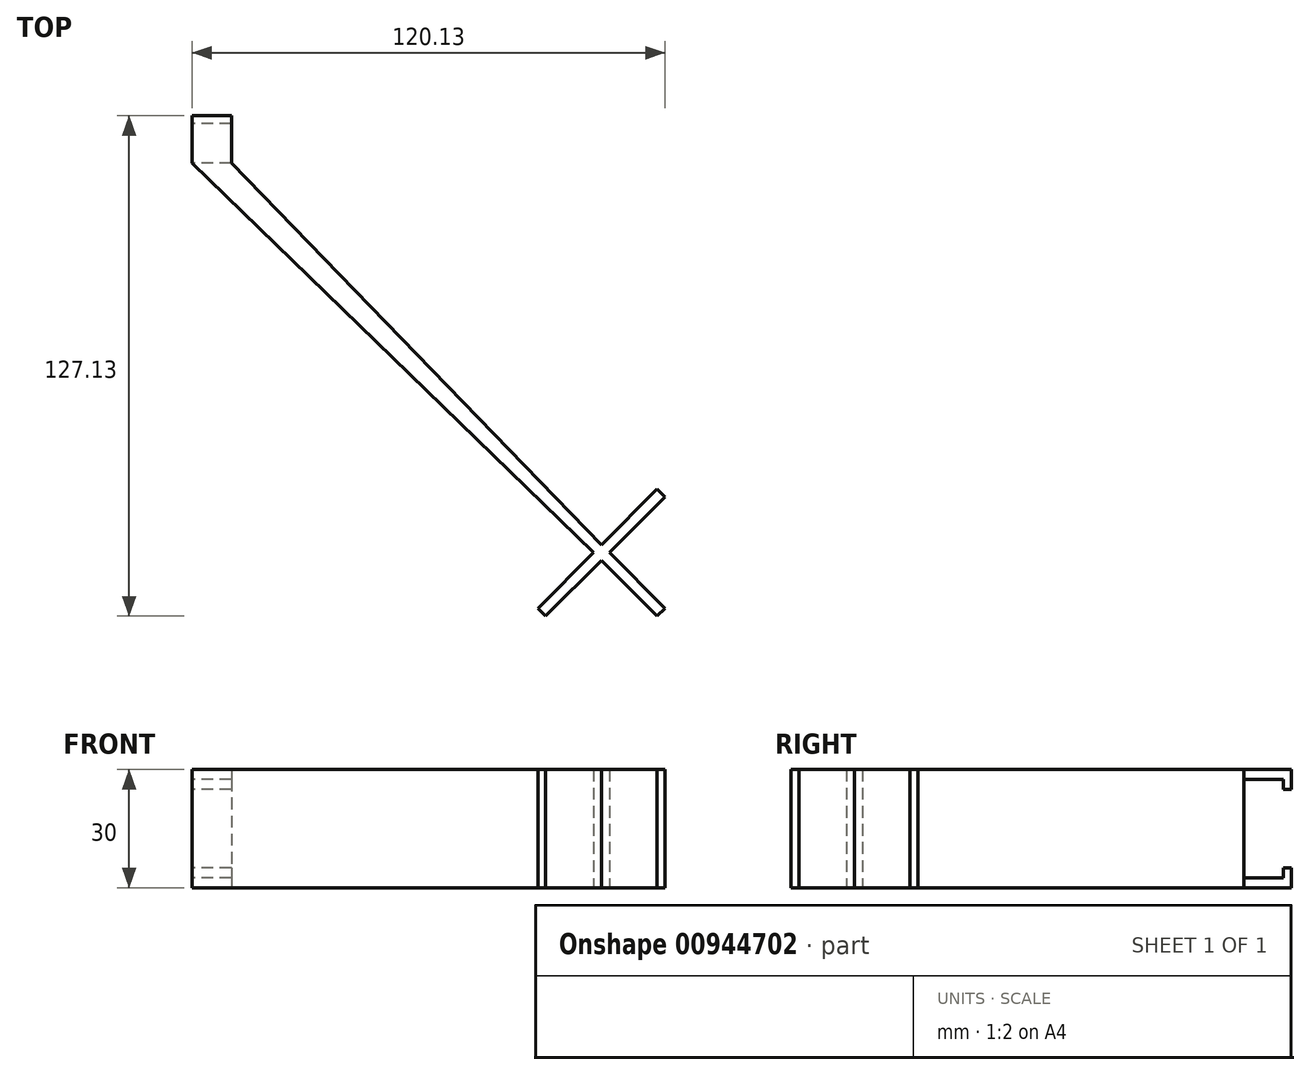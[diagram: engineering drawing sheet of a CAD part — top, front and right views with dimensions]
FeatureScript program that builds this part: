
annotation { "Feature Type Name" : "Feature", "Feature Type Description" : "" }
export const myFeature = defineFeature(function(context is Context, id is Id, definition is map)
    precondition{}
    {
        {
            var Q0;
            Q0=qCreatedBy(makeId("Top.planeOp"),FACE);
            var sketch = newSketch(context, id + "F0", { "sketchPlane" : qUnion([Q0])});
            skLineSegment(sketch, "E0", {"start": v(-104, 99) * mm, "end": v(-94, 99) * mm});
            skLineSegment(sketch, "E1", {"start": v(-94, 99) * mm, "end": v(0, 2) * mm});
            skLineSegment(sketch, "E2", {"start": v(0, 2) * mm, "end": v(14.14, 16.14) * mm});
            skLineSegment(sketch, "E3", {"start": v(14.14, 16.14) * mm, "end": v(16.14, 14.14) * mm});
            skLineSegment(sketch, "E4", {"start": v(16.14, 14.14) * mm, "end": v(2, 0) * mm});
            skLineSegment(sketch, "E5", {"start": v(2, 0) * mm, "end": v(16.14, -14.14) * mm});
            skLineSegment(sketch, "E6", {"start": v(16.14, -14.14) * mm, "end": v(14.14, -16.14) * mm});
            skLineSegment(sketch, "E7", {"start": v(14.14, -16.14) * mm, "end": v(0, -2) * mm});
            skLineSegment(sketch, "E8", {"start": v(0, -2) * mm, "end": v(-14.14, -16.14) * mm});
            skLineSegment(sketch, "E9", {"start": v(-14.14, -16.14) * mm, "end": v(-16.14, -14.14) * mm});
            skLineSegment(sketch, "E10", {"start": v(-16.14, -14.14) * mm, "end": v(-2, 0) * mm});
            skLineSegment(sketch, "E11", {"start": v(-2, 0) * mm, "end": v(-104, 99) * mm});
            skCircle(sketch, "E12", {"center": v(0, 0) * mm, "radius": 2 * mm, "construction": true});
            skLineSegment(sketch, "E13", {"start": v(0, -16.72) * mm, "end": v(0, 7.68) * mm, "construction": true});
            skLineSegment(sketch, "E14", {"start": v(-19.65, 0) * mm, "end": v(17.97, 0) * mm, "construction": true});
            skPoint(sketch, "E15", {"position": v(2, 0) * mm});
            skPoint(sketch, "E16", {"position": v(0, -2) * mm});
            skPoint(sketch, "E17", {"position": v(0, 2) * mm});
            skPoint(sketch, "E18", {"position": v(-2, 0) * mm});
            skLineSegment(sketch, "E19", {"start": v(-99, 99) * mm, "end": v(0, 0) * mm, "construction": true});
            skSolve(sketch);
        }
        {
            var Q0;
            Q0 = qSketchRegion(id + "F0", true);
            extrude(context, id + "F1", {"entities" : qUnion([Q0]), "depth" : 30 * mm, "offsetDistance" : 25 * mm});
        }
        {
            var Q0;
            Q0=makeQuery(id+"F1.opExtrude","SWEPT_FACE",FACE,{"disambiguationData":[OSD([sQuery(id+"F0.wireOp",EDGE,"E0")])]});
            var sketch = newSketch(context, id + "F2", { "sketchPlane" : qUnion([Q0])});
            skLineSegment(sketch, "E20.bottom", {"start": v(94, 0) * mm, "end": v(104, 0) * mm});
            skLineSegment(sketch, "E20.top", {"start": v(94, 2.5) * mm, "end": v(104, 2.5) * mm});
            skLineSegment(sketch, "E20.left", {"start": v(94, 0) * mm, "end": v(94, 2.5) * mm});
            skLineSegment(sketch, "E20.right", {"start": v(104, 0) * mm, "end": v(104, 2.5) * mm});
            skLineSegment(sketch, "E21.bottom", {"start": v(94, 30) * mm, "end": v(104, 30) * mm});
            skLineSegment(sketch, "E21.top", {"start": v(94, 27.5) * mm, "end": v(104, 27.5) * mm});
            skLineSegment(sketch, "E21.left", {"start": v(94, 30) * mm, "end": v(94, 27.5) * mm});
            skLineSegment(sketch, "E21.right", {"start": v(104, 30) * mm, "end": v(104, 27.5) * mm});
            skSolve(sketch);
        }
        {
            var Q0;
            Q0 = qSketchRegion(id + "F2", true);
            extrude(context, id + "F3", {"entities" : qUnion([Q0]), "operationType" : NewBodyOperationType.ADD, "depth" : 10 * mm, "offsetDistance" : 25 * mm});
        }
        {
            var Q0;
            Q0=makeQuery(id+"F3.opExtrude","CAP_FACE",FACE,{"disambiguationData":[OSD([sQuery(id+"F2.wireOp",EDGE,"E20.bottom"),sQuery(id+"F2.wireOp",EDGE,"E20.top"),sQuery(id+"F2.wireOp",EDGE,"E20.left"),sQuery(id+"F2.wireOp",EDGE,"E20.right")])],"isStart":false});
            var sketch = newSketch(context, id + "F4", { "sketchPlane" : qUnion([Q0])});
            skLineSegment(sketch, "E22.bottom", {"start": v(94, 0) * mm, "end": v(104, 0) * mm});
            skLineSegment(sketch, "E22.top", {"start": v(94, 5) * mm, "end": v(104, 5) * mm});
            skLineSegment(sketch, "E22.left", {"start": v(94, 0) * mm, "end": v(94, 5) * mm});
            skLineSegment(sketch, "E22.right", {"start": v(104, 0) * mm, "end": v(104, 5) * mm});
            skSolve(sketch);
        }
        {
            var Q0;
            Q0=makeQuery(id+"F3.opExtrude","CAP_FACE",FACE,{"disambiguationData":[OSD([sQuery(id+"F2.wireOp",EDGE,"E21.bottom"),sQuery(id+"F2.wireOp",EDGE,"E21.top"),sQuery(id+"F2.wireOp",EDGE,"E21.left"),sQuery(id+"F2.wireOp",EDGE,"E21.right")])],"isStart":false});
            var sketch = newSketch(context, id + "F5", { "sketchPlane" : qUnion([Q0])});
            skLineSegment(sketch, "E23.bottom", {"start": v(94, 30) * mm, "end": v(104, 30) * mm});
            skLineSegment(sketch, "E23.top", {"start": v(94, 25) * mm, "end": v(104, 25) * mm});
            skLineSegment(sketch, "E23.left", {"start": v(94, 30) * mm, "end": v(94, 25) * mm});
            skLineSegment(sketch, "E23.right", {"start": v(104, 30) * mm, "end": v(104, 25) * mm});
            skSolve(sketch);
        }
        {
            var Q0;
            Q0 = qSketchRegion(id + "F4", true);
            var Q1;
            Q1 = qSketchRegion(id + "F5", true);
            extrude(context, id + "F6", {"entities" : qUnion([Q0, Q1]), "operationType" : NewBodyOperationType.ADD, "depth" : 2 * mm, "offsetDistance" : 25 * mm});
        }
    });
